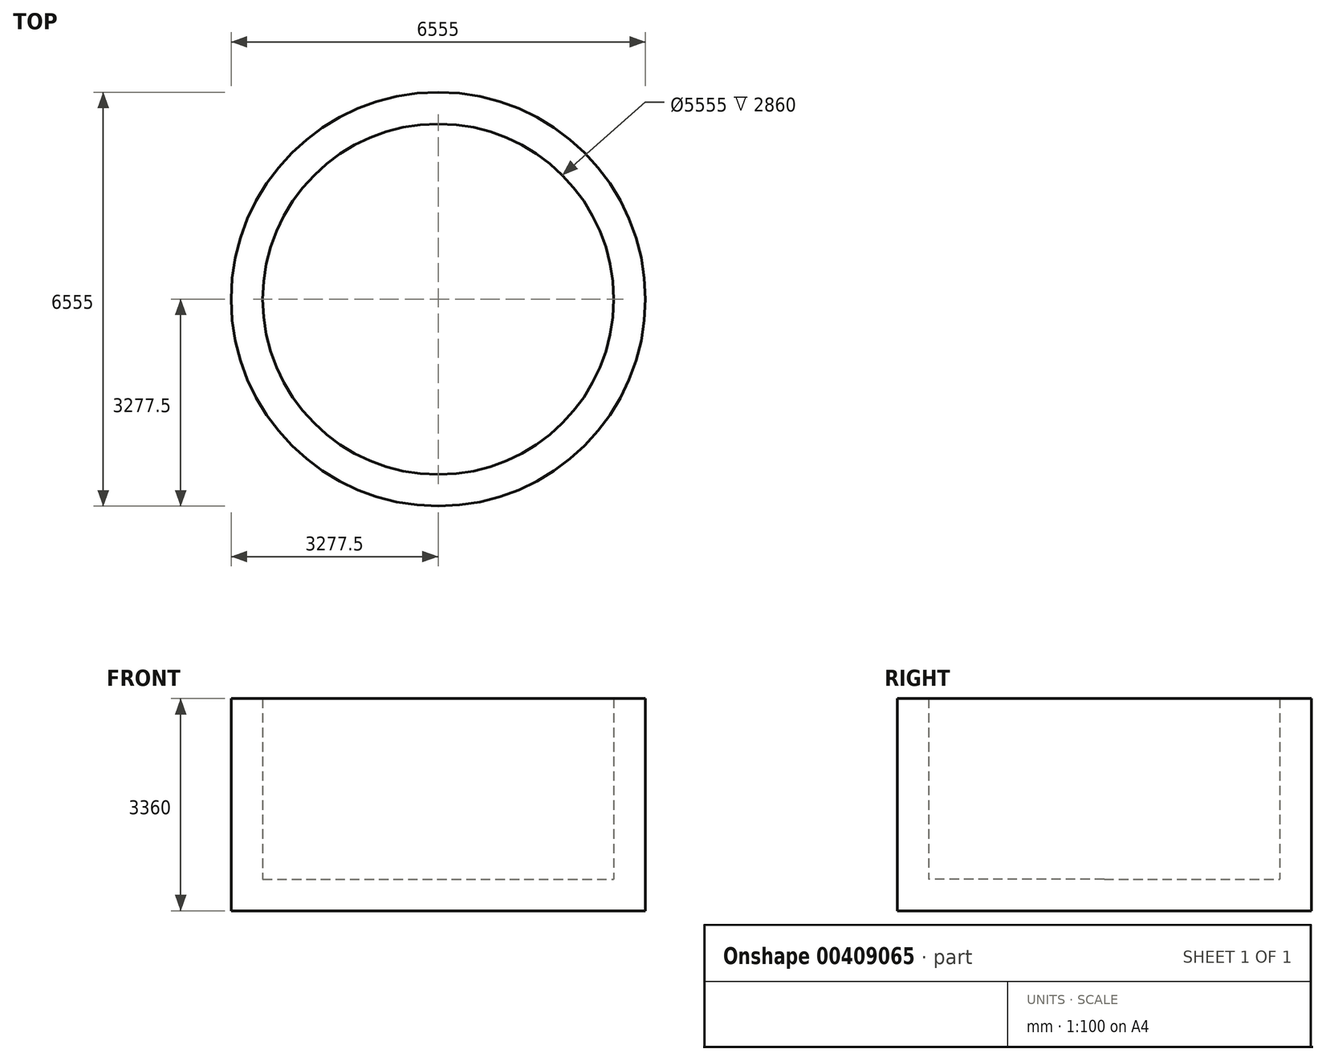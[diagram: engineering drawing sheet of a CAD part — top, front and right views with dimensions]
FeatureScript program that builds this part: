
annotation { "Feature Type Name" : "Feature", "Feature Type Description" : "" }
export const myFeature = defineFeature(function(context is Context, id is Id, definition is map)
    precondition{}
    {
        {
            var Q0;
            Q0=qCreatedBy(makeId("Front.planeOp"),FACE);
            var sketch = newSketch(context, id + "F0", { "sketchPlane" : qUnion([Q0])});
            skLineSegment(sketch, "E0", {"start": v(-3277.5, 0) * mm, "end": v(3277.5, 0) * mm});
            skLineSegment(sketch, "E1", {"start": v(-3277.5, 0) * mm, "end": v(-3277.5, 3360) * mm});
            skLineSegment(sketch, "E2.bottom", {"start": v(3277.5, 0) * mm, "end": v(-3277.5, 0) * mm});
            skLineSegment(sketch, "E2.top", {"start": v(3277.5, 3360) * mm, "end": v(-3277.5, 3360) * mm});
            skLineSegment(sketch, "E2.left", {"start": v(3277.5, 0) * mm, "end": v(3277.5, 3360) * mm});
            skLineSegment(sketch, "E3", {"start": v(0, 0) * mm, "end": v(0, 3360) * mm});
            skSolve(sketch);
        }
        {
            var Q0;
            {var subQ0=sQuery(id+"F0.wireOp",EDGE,"E1");Q0=makeQuery(id+"F0.imprint","IMPRINT",FACE,{"disambiguationData":[TD([[makeQuery(id+"F0.imprint","IMPRINT",EDGE,{"derivedFrom":subQ0}),-1.0]])]});}
            var Q1;
            Q1=sQuery(id+"F0.wireOp",EDGE,"E3");
            revolve(context, id + "F1", {"entities" : qUnion([Q0]), "axis" : qUnion([Q1]), "revolveType" : RevolveType.FULL});
        }
        {
            var Q0;
            Q0=makeQuery(id+"F1.opRevolve","SWEPT_FACE",FACE,{"disambiguationData":[OSD([sQuery(id+"F0.wireOp",EDGE,"E2.top")])]});
            shell(context, id + "F2", {"entities" : qUnion([Q0]), "thickness" : 500 * mm});
        }
    });
